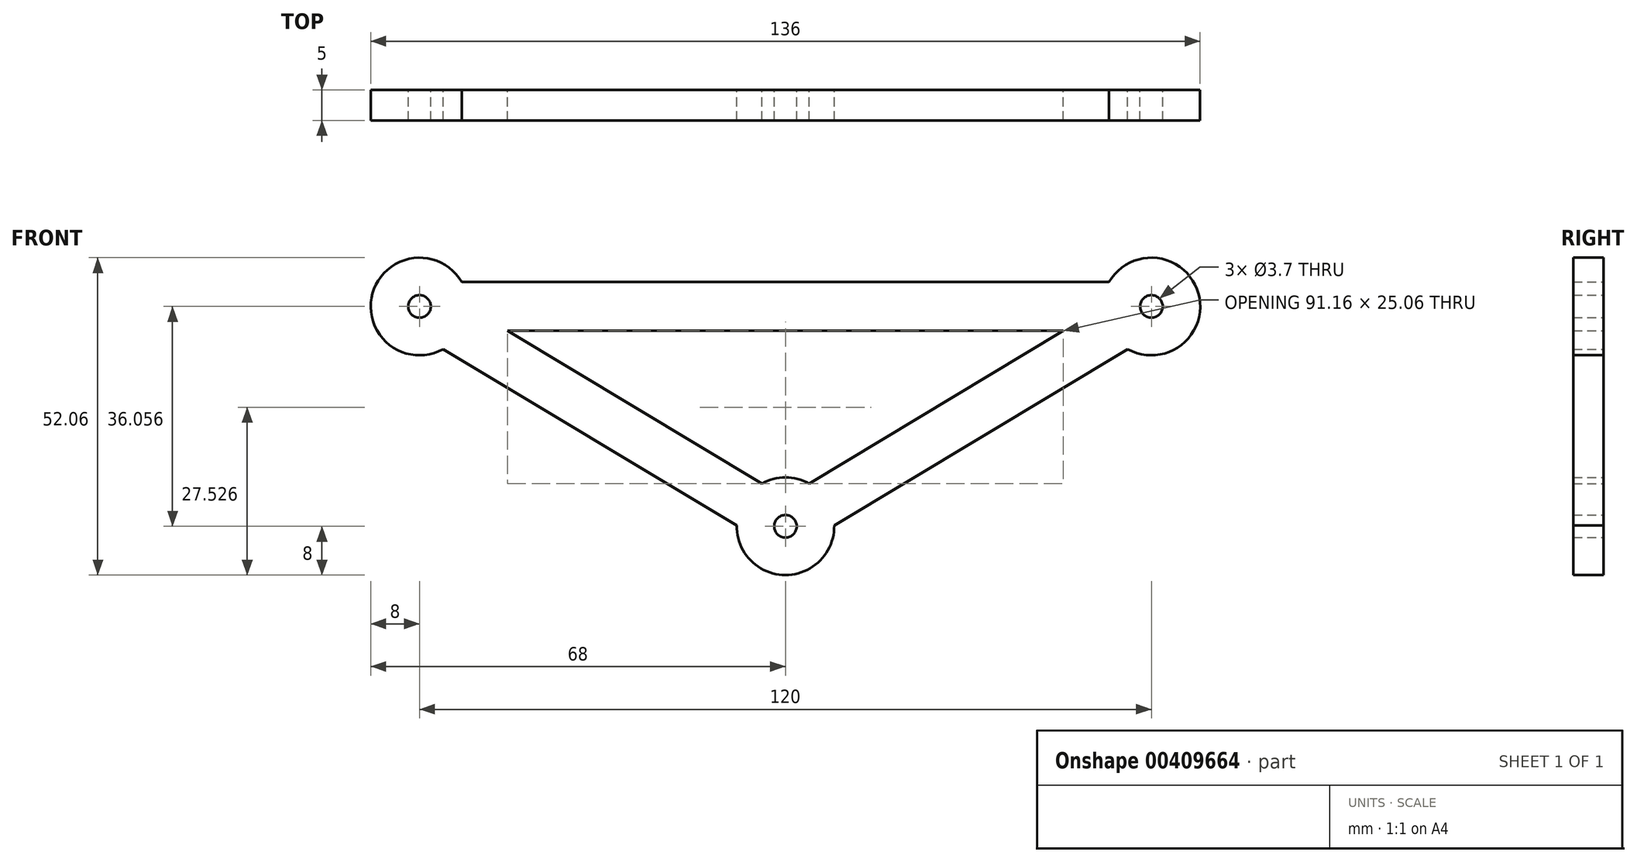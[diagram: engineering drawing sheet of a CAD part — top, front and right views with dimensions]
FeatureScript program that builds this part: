
annotation { "Feature Type Name" : "Feature", "Feature Type Description" : "" }
export const myFeature = defineFeature(function(context is Context, id is Id, definition is map)
    precondition{}
    {
        {
            var Q0;
            Q0=qCreatedBy(makeId("Front.planeOp"),FACE);
            var sketch = newSketch(context, id + "F0", { "sketchPlane" : qUnion([Q0])});
            skArc(sketch, "E0", {"start": v(-8, 0.14) * mm, "mid": v(0, -8) * mm, "end": v(8, 0.14) * mm});
            skArc(sketch, "E1", {"start": v(-53.07, 40.06) * mm, "mid": v(-67.7, 38.2) * mm, "end": v(-56.12, 29.06) * mm});
            skArc(sketch, "E2", {"start": v(56.12, 29.06) * mm, "mid": v(67.7, 38.2) * mm, "end": v(53.07, 40.06) * mm});
            skLineSegment(sketch, "E3.bottom", {"start": v(45.58, 32.06) * mm, "end": v(-45.58, 32.06) * mm});
            skLineSegment(sketch, "E3.top", {"start": v(53.07, 40.06) * mm, "end": v(-53.07, 40.06) * mm});
            skPoint(sketch, "E3.middle", {"position": v(0, 36.06) * mm});
            skLineSegment(sketch, "E4", {"start": v(-3.88, 7) * mm, "end": v(-45.58, 32.06) * mm});
            skLineSegment(sketch, "E5", {"start": v(-56.12, 29.06) * mm, "end": v(-7.77, 0) * mm});
            skLineSegment(sketch, "E6.MirrorCS", {"start": v(3.88, 7) * mm, "end": v(45.58, 32.06) * mm});
            skLineSegment(sketch, "E7.MirrorCS", {"start": v(56.12, 29.06) * mm, "end": v(7.77, 0) * mm});
            skArc(sketch, "E8.trimOffspring", {"start": v(3.88, 7) * mm, "mid": v(0, 8) * mm, "end": v(-3.88, 7) * mm});
            skCircle(sketch, "E9", {"center": v(-60, 36.06) * mm, "radius": 1.85 * mm});
            skCircle(sketch, "E10", {"center": v(0, 0) * mm, "radius": 1.85 * mm});
            skCircle(sketch, "E11", {"center": v(60, 36.06) * mm, "radius": 1.85 * mm});
            skSolve(sketch);
        }
        {
            var Q0;
            {var subQ1=sQuery(id+"F0.wireOp",EDGE,"E0");Q0=makeQuery(id+"F0.imprint","IMPRINT",FACE,{"disambiguationData":[TD([[makeQuery(id+"F0.imprint","IMPRINT",EDGE,{"derivedFrom":subQ1}),1.0]])]});}
            extrude(context, id + "F1", {"entities" : qUnion([Q0]), "endBound" : BoundingType.SYMMETRIC, "depth" : 5 * mm});
        }
    });
